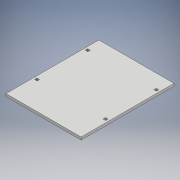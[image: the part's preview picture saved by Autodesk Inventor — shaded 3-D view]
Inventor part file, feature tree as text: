
AUTODESK INVENTOR PART (.ipt)
format: ipt  version: 2018 (Build 220112000, 112)  size: 116,736 bytes
history: native  units: mm
features: extrude x1, sketch x1
ambient origin geometry x8: Origin, YZ Plane, XZ Plane, XY Plane, X Axis, Y Axis, Z Axis, Center Point
bodies: Solid1 (feature_tree)
feature tree (2):
  extrude  "Extrusion1"  Depth=3.0mm
  sketch  "Sketch1"  dims[d0=3.0mm d1=3.0mm d2=4.0mm d3=0.0mm]
